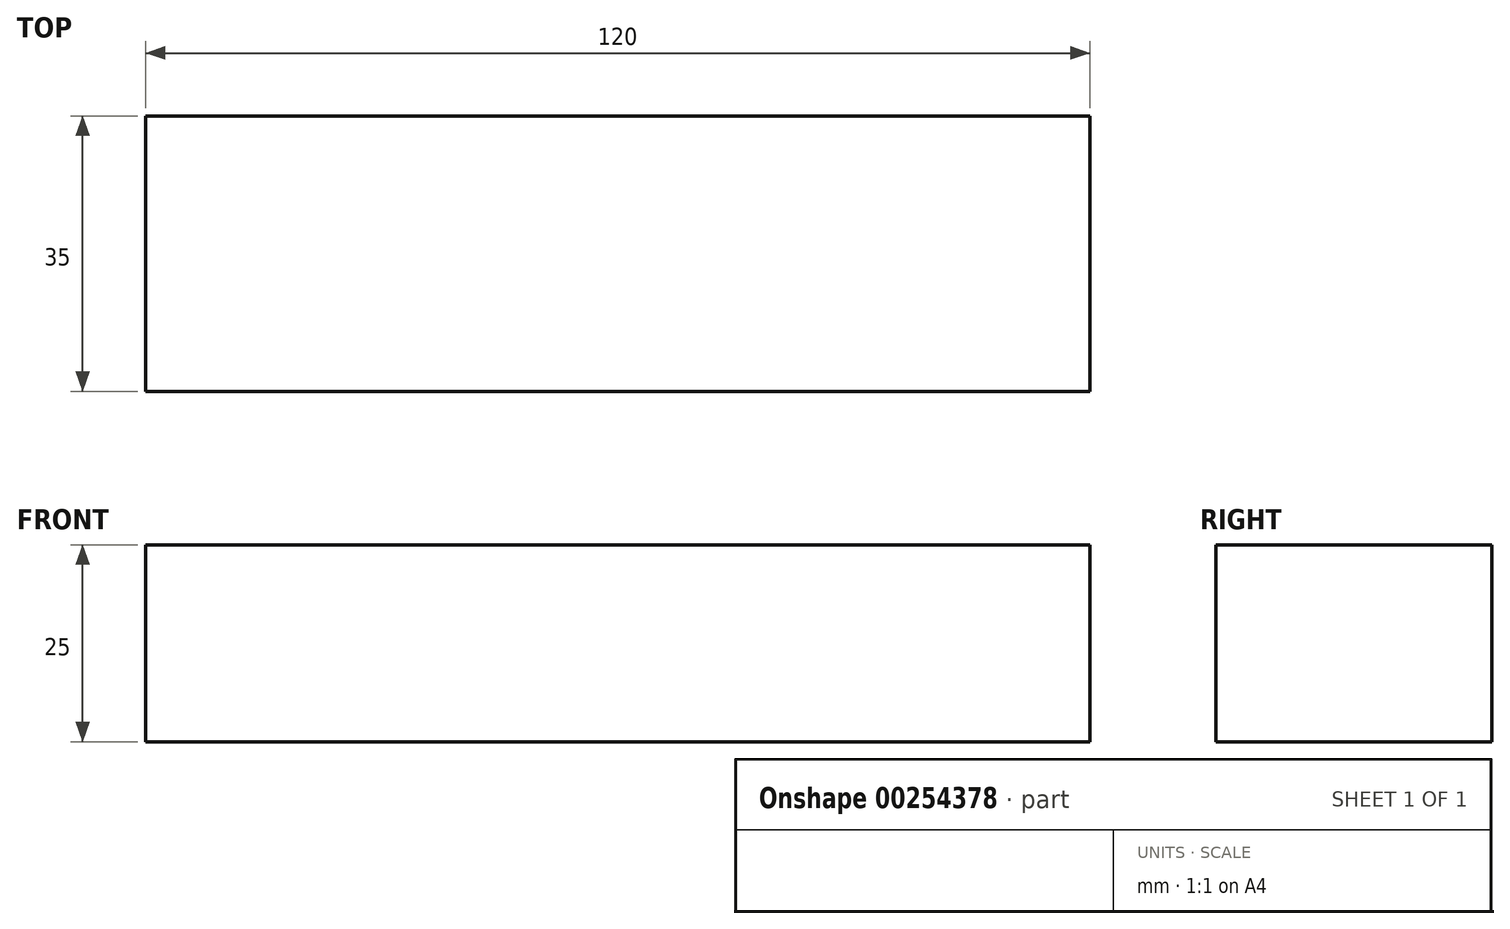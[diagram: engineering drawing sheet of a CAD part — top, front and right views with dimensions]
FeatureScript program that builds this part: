
annotation { "Feature Type Name" : "Feature", "Feature Type Description" : "" }
export const myFeature = defineFeature(function(context is Context, id is Id, definition is map)
    precondition{}
    {
        {
            var Q0;
            Q0=qCreatedBy(makeId("Top.planeOp"),FACE);
            var sketch = newSketch(context, id + "F0", { "sketchPlane" : qUnion([Q0])});
            skLineSegment(sketch, "E0.bottom", {"start": v(60, 17.5) * mm, "end": v(-60, 17.5) * mm});
            skLineSegment(sketch, "E0.top", {"start": v(60, -17.5) * mm, "end": v(-60, -17.5) * mm});
            skLineSegment(sketch, "E0.left", {"start": v(60, 17.5) * mm, "end": v(60, -17.5) * mm});
            skLineSegment(sketch, "E0.right", {"start": v(-60, 17.5) * mm, "end": v(-60, -17.5) * mm});
            skPoint(sketch, "E0.middle", {"position": v(0, 0) * mm});
            skSolve(sketch);
        }
        {
            var Q0;
            Q0 = qSketchRegion(id + "F0", true);
            extrude(context, id + "F1", {"entities" : qUnion([Q0]), "depth" : 25 * mm});
        }
    });
